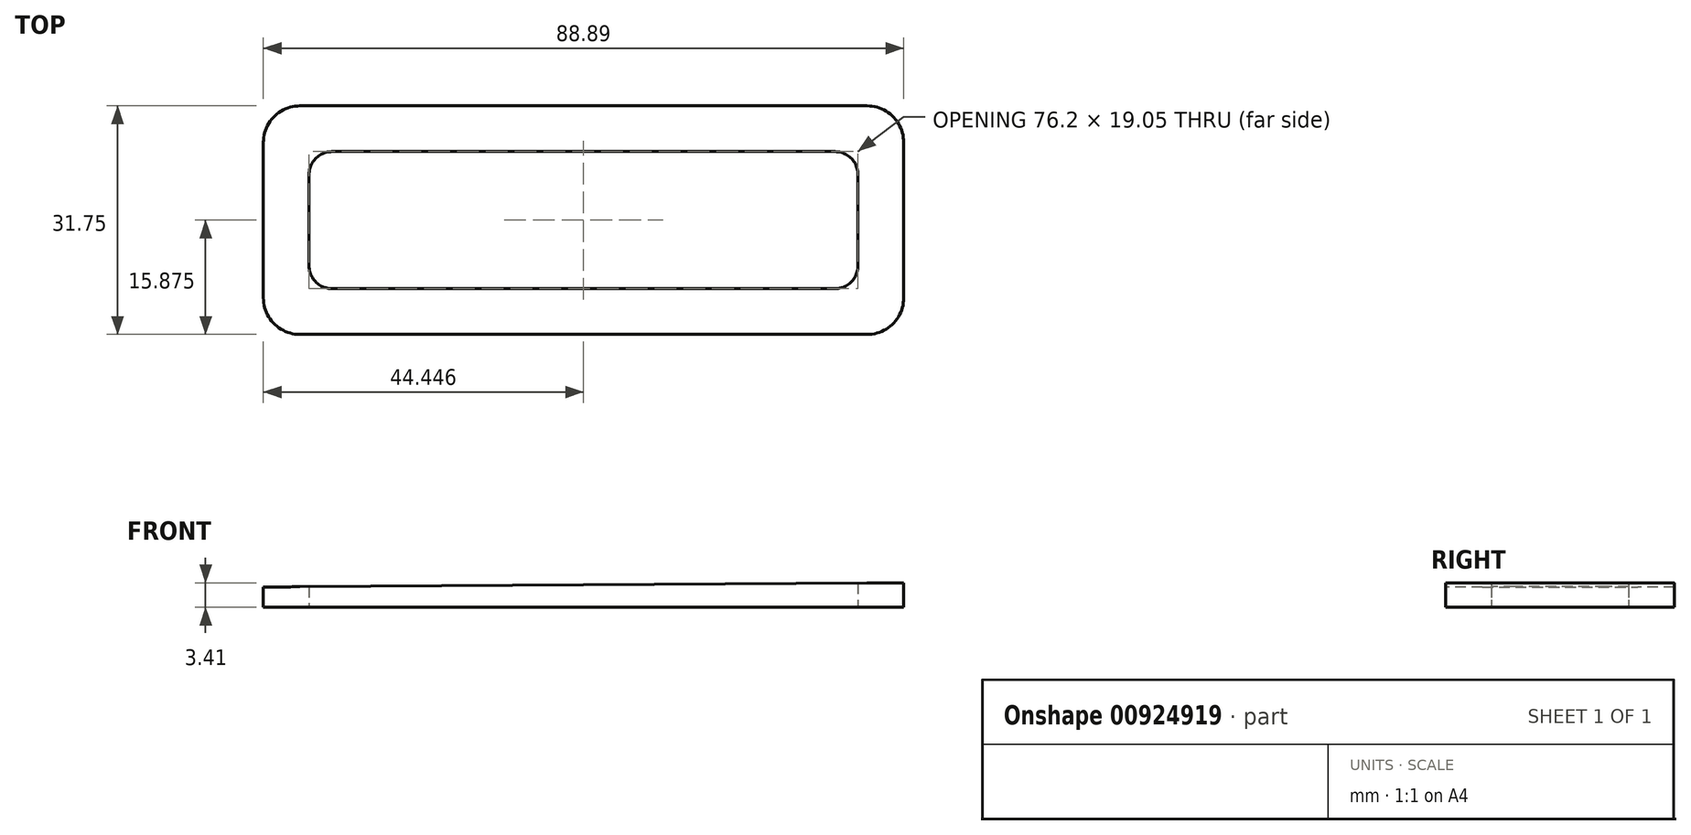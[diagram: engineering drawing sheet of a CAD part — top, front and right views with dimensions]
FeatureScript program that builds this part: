
annotation { "Feature Type Name" : "Feature", "Feature Type Description" : "" }
export const myFeature = defineFeature(function(context is Context, id is Id, definition is map)
    precondition{}
    {
        {
            var Q0;
            Q0=qCreatedBy(makeId("Front.planeOp"),FACE);
            var sketch = newSketch(context, id + "F0", { "sketchPlane" : qUnion([Q0])});
            skLineSegment(sketch, "E0", {"start": v(0, 0) * mm, "end": v(0, 1.59) * mm});
            skLineSegment(sketch, "E1", {"start": v(0, 1.59) * mm, "end": v(609.6, 5.56) * mm});
            skLineSegment(sketch, "E2", {"start": v(609.6, 5.56) * mm, "end": v(609.6, 0) * mm});
            skLineSegment(sketch, "E3", {"start": v(609.6, 0) * mm, "end": v(0, 0) * mm});
            skSolve(sketch);
        }
        {
            var Q0;
            Q0=qCreatedBy(makeId("Front.planeOp"),FACE);
            var sketch = newSketch(context, id + "F1", { "sketchPlane" : qUnion([Q0])});
            skLineSegment(sketch, "E4", {"start": v(609.6, 5.56) * mm, "end": v(520.7, 4.98) * mm});
            skLineSegment(sketch, "E5", {"start": v(520.7, 4.98) * mm, "end": v(520.7, 0) * mm});
            skLineSegment(sketch, "E6", {"start": v(520.7, 0) * mm, "end": v(609.6, 0) * mm});
            skLineSegment(sketch, "E7", {"start": v(609.6, 0) * mm, "end": v(609.6, 5.56) * mm});
            skSolve(sketch);
        }
        {
            var Q0;
            Q0=qCreatedBy(makeId("Front.planeOp"),FACE);
            var sketch = newSketch(context, id + "F2", { "sketchPlane" : qUnion([Q0])});
            skLineSegment(sketch, "E8", {"start": v(444.5, 4.48) * mm, "end": v(444.5, 0) * mm});
            skLineSegment(sketch, "E9", {"start": v(444.5, 0) * mm, "end": v(355.6, 0) * mm});
            skLineSegment(sketch, "E10", {"start": v(-243.84, 0) * mm, "end": v(-243.84, 0) * mm});
            skLineSegment(sketch, "E11", {"start": v(355.57, 3.9) * mm, "end": v(444.5, 4.48) * mm});
            skLineSegment(sketch, "E12", {"start": v(355.57, 3.9) * mm, "end": v(355.6, 0) * mm});
            skSolve(sketch);
        }
        {
            var Q0;
            Q0=makeQuery(id+"F0.imprint","IMPRINT",FACE,{"disambiguationData":[TD([[makeQuery(id+"F0.imprint","IMPRINT",EDGE,{"derivedFrom":sQuery(id+"F0.wireOp",EDGE,"E0")}),-1.0]])]});
            var sketch = newSketch(context, id + "F3", { "sketchPlane" : qUnion([Q0])});
            skLineSegment(sketch, "E13", {"start": v(279.37, 3.4) * mm, "end": v(279.37, 0) * mm});
            skLineSegment(sketch, "E14", {"start": v(279.37, 0) * mm, "end": v(190.48, 0) * mm});
            skLineSegment(sketch, "E15", {"start": v(190.48, 0) * mm, "end": v(190.48, 2.83) * mm});
            skLineSegment(sketch, "E16", {"start": v(190.48, 2.83) * mm, "end": v(279.37, 3.4) * mm});
            skSolve(sketch);
        }
        {
            var Q0;
            Q0 = qSketchRegion(id + "F3", true);
            extrude(context, id + "F4", {"entities" : qUnion([Q0]), "depth" : 31.75 * mm, "offsetDistance" : 25.4 * mm});
        }
        {
            var Q0;
            Q0=makeQuery(id+"F4.opExtrude","SWEPT_FACE",FACE,{"disambiguationData":[OSD([sQuery(id+"F3.wireOp",EDGE,"E14")])]});
            var sketch = newSketch(context, id + "F5", { "sketchPlane" : qUnion([Q0])});
            skLineSegment(sketch, "E17.bottom", {"start": v(200, 25.4) * mm, "end": v(269.85, 25.4) * mm});
            skLineSegment(sketch, "E17.top", {"start": v(200, 6.35) * mm, "end": v(269.85, 6.35) * mm});
            skLineSegment(sketch, "E17.left", {"start": v(196.83, 22.22) * mm, "end": v(196.83, 9.53) * mm});
            skLineSegment(sketch, "E17.right", {"start": v(273.02, 22.23) * mm, "end": v(273.02, 9.53) * mm});
            skPoint(sketch, "E18.visualSharp", {"position": v(196.83, 25.4) * mm});
            skArc(sketch, "E18.filletArc", {"start": v(200, 25.4) * mm, "mid": v(197.76, 24.47) * mm, "end": v(196.83, 22.22) * mm});
            skPoint(sketch, "E19.visualSharp", {"position": v(273.02, 25.4) * mm});
            skArc(sketch, "E19.filletArc", {"start": v(273.02, 22.23) * mm, "mid": v(272.1, 24.47) * mm, "end": v(269.85, 25.4) * mm});
            skPoint(sketch, "E20.visualSharp", {"position": v(273.02, 6.35) * mm});
            skArc(sketch, "E20.filletArc", {"start": v(269.85, 6.35) * mm, "mid": v(272.1, 7.28) * mm, "end": v(273.02, 9.53) * mm});
            skPoint(sketch, "E21.visualSharp", {"position": v(196.83, 6.35) * mm});
            skArc(sketch, "E21.filletArc", {"start": v(196.83, 9.53) * mm, "mid": v(197.76, 7.28) * mm, "end": v(200, 6.35) * mm});
            skSolve(sketch);
        }
        {
            var Q0;
            Q0=makeQuery(id+"F5.imprint","IMPRINT",FACE,{"disambiguationData":[TD([[makeQuery(id+"F5.imprint","IMPRINT",EDGE,{"derivedFrom":sQuery(id+"F5.wireOp",EDGE,"E17.bottom")}),-1.0]])]});
            extrude(context, id + "F6", {"entities" : qUnion([Q0]), "operationType" : NewBodyOperationType.REMOVE, "endBound" : BoundingType.THROUGH_ALL, "oppositeDirection" : true, "depth" : 25.4 * mm, "offsetDistance" : 25.4 * mm});
        }
        {
            var Q0;
            Q0=makeQuery(id+"F4.opExtrude","CAP_EDGE",EDGE,{"disambiguationData":[OSD([sQuery(id+"F3.wireOp",EDGE,"E13")])],"isStart":false});
            var Q1;
            Q1=makeQuery(id+"F4.opExtrude","CAP_EDGE",EDGE,{"disambiguationData":[OSD([sQuery(id+"F3.wireOp",EDGE,"E15")])],"isStart":false});
            var Q2;
            Q2=makeQuery(id+"F4.opExtrude","CAP_EDGE",EDGE,{"disambiguationData":[OSD([sQuery(id+"F3.wireOp",EDGE,"E15")])],"isStart":true});
            var Q3;
            Q3=makeQuery(id+"F4.opExtrude","CAP_EDGE",EDGE,{"disambiguationData":[OSD([sQuery(id+"F3.wireOp",EDGE,"E13")])],"isStart":true});
            fillet(context, id + "F7", {"entities" : qUnion([Q0, Q1, Q2, Q3]), "radius" : 5.08 * mm, "tangentPropagation" : true, "allowEdgeOverflow" : false});
        }
    });
